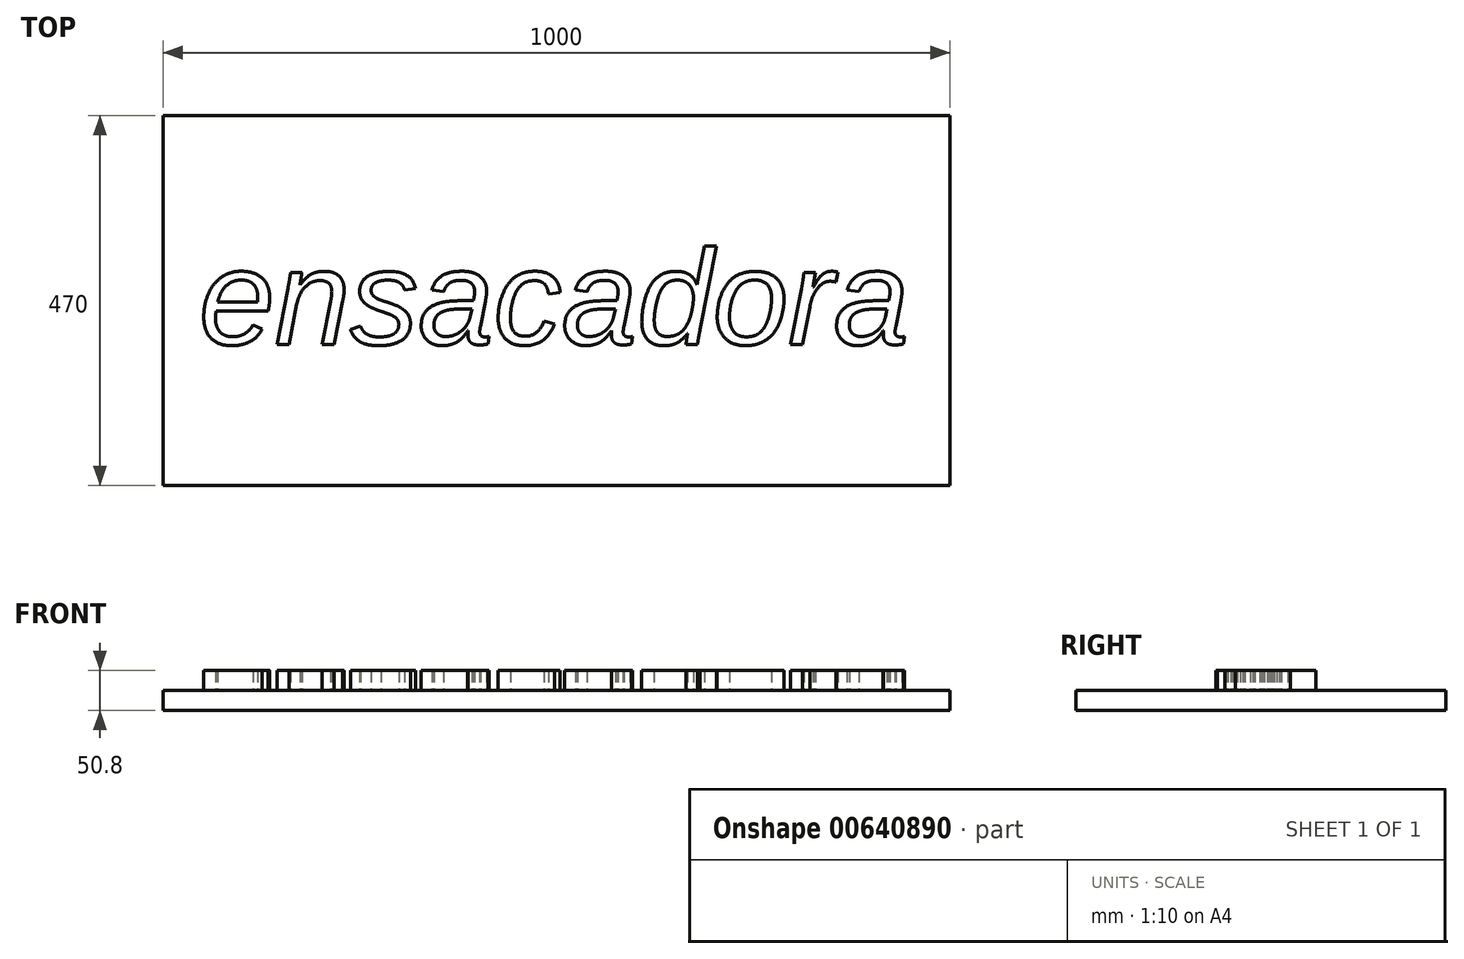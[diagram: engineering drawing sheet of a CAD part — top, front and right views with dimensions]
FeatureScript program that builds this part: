
annotation { "Feature Type Name" : "Feature", "Feature Type Description" : "" }
export const myFeature = defineFeature(function(context is Context, id is Id, definition is map)
    precondition{}
    {
        {
            var Q0;
            Q0=qCreatedBy(makeId("Top.planeOp"),FACE);
            var sketch = newSketch(context, id + "F0", { "sketchPlane" : qUnion([Q0])});
            skLineSegment(sketch, "E0.bottom", {"start": v(-500, 235) * mm, "end": v(500, 235) * mm});
            skLineSegment(sketch, "E0.top", {"start": v(-500, -235) * mm, "end": v(500, -235) * mm});
            skLineSegment(sketch, "E0.left", {"start": v(-500, 235) * mm, "end": v(-500, -235) * mm});
            skLineSegment(sketch, "E0.right", {"start": v(500, 235) * mm, "end": v(500, -235) * mm});
            skLineSegment(sketch, "E1", {"start": v(0, 313.73) * mm, "end": v(0, -302.34) * mm, "construction": true});
            skLineSegment(sketch, "E2", {"start": v(-664.04, 0) * mm, "end": v(880.98, 0) * mm, "construction": true});
            skSolve(sketch);
        }
        {
            var Q0;
            Q0 = qSketchRegion(id + "F0", true);
            extrude(context, id + "F1", {"entities" : qUnion([Q0]), "depth" : 25.4 * mm, "offsetDistance" : 25.4 * mm});
        }
        {
            var Q0;
            Q0=makeQuery(id+"F1.opExtrude","CAP_FACE",FACE,{"disambiguationData":[OSD([sQuery(id+"F0.wireOp",EDGE,"E0.bottom"),sQuery(id+"F0.wireOp",EDGE,"E0.top"),sQuery(id+"F0.wireOp",EDGE,"E0.left"),sQuery(id+"F0.wireOp",EDGE,"E0.right")])],"isStart":false});
            var sketch = newSketch(context, id + "F2", { "sketchPlane" : qUnion([Q0])});
            skText(sketch, "E3", { "text": "ensacadora ", "fontName": "Arimo-Italic.ttf"});
            const initialGuessF2  = {"E3": [-0.45393, -0.05573, 1, 0, 0.12425]};
            skSetInitialGuess(sketch, initialGuessF2);
            skSolve(sketch);
        }
        {
            var Q0;
            Q0 = qSketchRegion(id + "F2", true);
            extrude(context, id + "F3", {"entities" : qUnion([Q0]), "operationType" : NewBodyOperationType.ADD, "depth" : 25.4 * mm, "offsetDistance" : 25.4 * mm});
        }
    });
